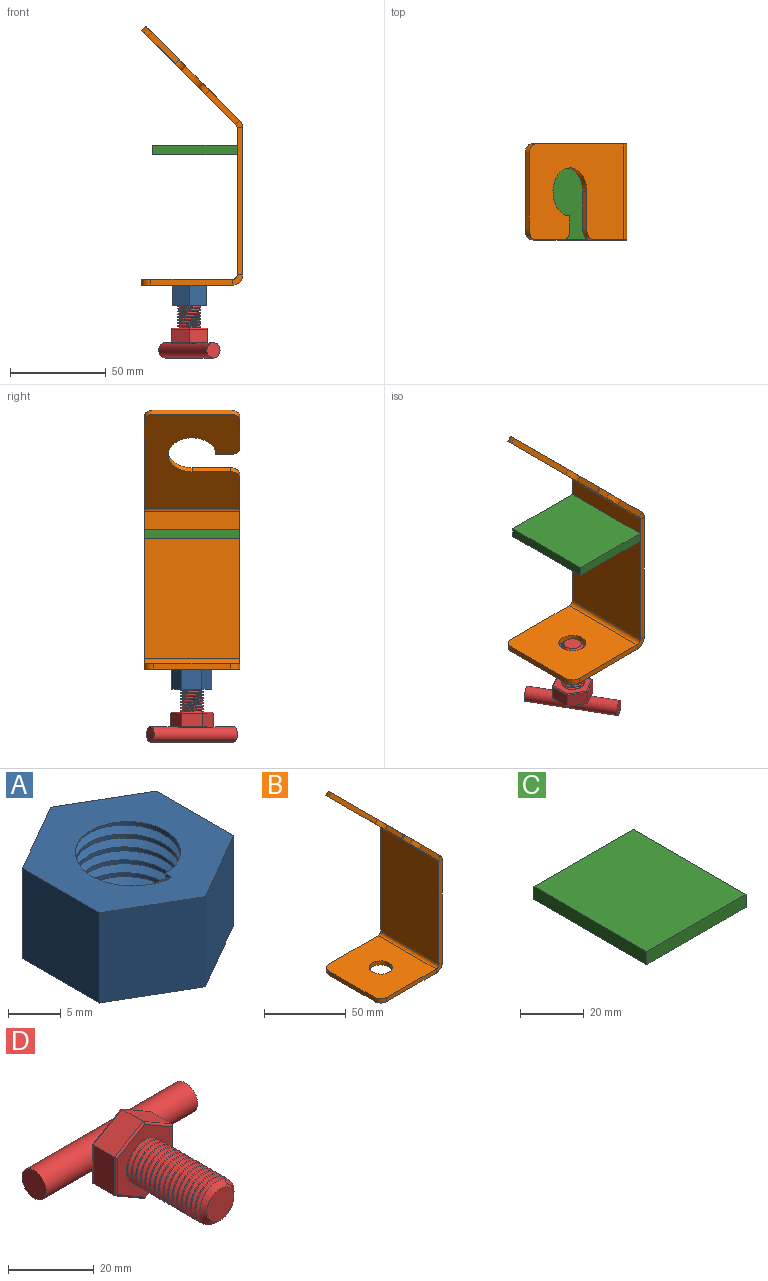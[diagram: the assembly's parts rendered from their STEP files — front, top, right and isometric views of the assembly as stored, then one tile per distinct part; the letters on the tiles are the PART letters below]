
ASSEMBLY  parts=4 mates=5
PART A: 13 faces, bbox 18.5x21.3x12.5 mm
  f0: cylinder r=5mm len=10.5mm, axis (0,0,-1), area 102.1mm2, adj f1,f8,f9,f10,f11,f12
  f1: plane 21.32x18.54mm, normal (0,0,-1), area 196.9mm2, adj f0,f2,f3,f4,f5,f6,f7,f9
  f2: plane 10.5x9mm, normal (-0.5,0.87,0), area 109.1mm2, adj f1,f3,f7,f8
  f3: plane 10.5x10.39mm, normal (-1,0,0), area 109.1mm2, adj f1,f2,f4,f8
  f4: plane 10.5x9mm, normal (-0.5,-0.87,0), area 109.1mm2, adj f1,f3,f5,f8
  f5: plane 10.5x9mm, normal (0.5,-0.87,0), area 109.1mm2, adj f1,f4,f6,f8
  f6: plane 10.5x10.39mm, normal (1,0,0), area 109.1mm2, adj f1,f5,f7,f8
  f7: plane 10.5x9mm, normal (0.5,0.87,0), area 109.1mm2, adj f1,f2,f6,f8
  f8: plane 21.32x18.54mm, normal (0,0,1), area 196.9mm2, adj f0,f2,f3,f4,f5,f6,f7,f10
  f9: plane 0.9x0.52mm, normal (1,0,0), area 0.2mm2, adj f0,f1,f11
  f10: plane 0.9x0.52mm, normal (-1,0,0), area 0.2mm2, adj f0,f8,f12
  f11: bspline ~13.63x11.8mm, area 243mm2, adj f0,f8,f9,f12
  f12: bspline ~13.63x11.8mm, area 240.1mm2, adj f0,f1,f10,f11
PART B: 33 faces, bbox 53x50x135.1 mm
  f0: plane 42.7x3mm, normal (0,-1,0), area 128.1mm2, adj f4,f5,f6,f30
  f1: plane 40x3mm, normal (-1,0,0), area 120mm2, adj f4,f5,f6,f7
  f2: plane 42.7x3mm, normal (0,1,0), area 128.1mm2, adj f4,f5,f7,f29
  f3: cylinder r=7mm len=14mm, axis (0,0,1), area 131.9mm2, adj f4,f5
  f4: plane 50x47.7mm, normal (0,0,-1), area 2220.3mm2, adj f0,f1,f2,f3,f6,f7,f31
  f5: plane 50x47.7mm, normal (0,0,1), area 2220.3mm2, adj f0,f1,f2,f3,f6,f7,f32
  f6: cylinder r=5mm len=5mm, axis (0,0,1), area 23.6mm2, adj f0,f1,f4,f5
  f7: cylinder r=5mm len=5mm, axis (0,0,-1), area 23.6mm2, adj f1,f2,f4,f5
  f8: plane 76.75x3mm, normal (0,-1,0), area 230.2mm2, adj f10,f11,f26,f30
  f9: plane 76.75x3mm, normal (0,1,0), area 230.2mm2, adj f10,f11,f25,f29
  f10: plane 76.75x50mm, normal (1,0,0), area 3837.4mm2, adj f8,f9,f27,f31
  f11: plane 76.75x50mm, normal (-1,0,0), area 3837.4mm2, adj f8,f9,f28,f32
  f12: plane 47.91x47.91mm, normal (0,1,0), area 194.3mm2, adj f19,f20,f21,f25
  f13: plane 40x2.12mm, normal (-0.71,0,0.71), area 120mm2, adj f19,f20,f21,f22
  f14: plane 16.26x16.26mm, normal (0,-1,0), area 60mm2, adj f19,f20,f22,f24
  f15: plane 7.5x2.12mm, normal (0.71,0,-0.71), area 22.5mm2, adj f16,f19,f20,f24
  f16: cylinder r=12.5mm len=25mm, axis (-0.71,0,-0.71), area 176.7mm2, adj f15,f17,f19,f20
  f17: plane 20x2.12mm, normal (-0.71,0,0.71), area 60mm2, adj f16,f19,f20,f23
  f18: plane 17.86x17.86mm, normal (0,-1,0), area 66.8mm2, adj f19,f20,f23,f26
  f19: plane 50x49.33mm, normal (0.71,0,0.71), area 2785.8mm2, adj f12,f13,f14,f15,f16,f17,f18,f21
  f20: plane 50x49.33mm, normal (-0.71,0,-0.71), area 2785.8mm2, adj f12,f13,f14,f15,f16,f17,f18,f21
  f21: cylinder r=5mm len=5.66mm, axis (-0.71,0,-0.71), area 23.6mm2, adj f12,f13,f19,f20
  f22: cylinder r=5mm len=5.66mm, axis (0.71,0,0.71), area 23.6mm2, adj f13,f14,f19,f20
  f23: cylinder r=5mm len=5.66mm, axis (0.71,0,0.71), area 23.6mm2, adj f17,f18,f19,f20
  f24: cylinder r=5mm len=5.66mm, axis (-0.71,0,-0.71), area 23.6mm2, adj f14,f15,f19,f20
  f25: plane 3.75x3.67mm, normal (0,1,0), area 9mm2, adj f9,f12,f27,f28
  f26: plane 3.75x3.67mm, normal (0,-1,0), area 9mm2, adj f8,f18,f27,f28
  f27: cylinder r=5.3mm len=50mm, axis (0,1,0), area 208.1mm2, adj f10,f19,f25,f26
  f28: cylinder r=2.3mm len=50mm, axis (0,1,0), area 90.3mm2, adj f11,f20,f25,f26
  f29: plane 5.3x5.3mm, normal (0,1,0), area 17.9mm2, adj f2,f9,f31,f32
  f30: plane 5.3x5.3mm, normal (0,-1,0), area 17.9mm2, adj f0,f8,f31,f32
  f31: cylinder r=5.3mm len=50mm, axis (0,1,0), area 416.3mm2, adj f4,f10,f29,f30
  f32: cylinder r=2.3mm len=50mm, axis (0,1,0), area 180.6mm2, adj f5,f11,f29,f30
PART C: 6 faces, bbox 43.9x50x5 mm
  f0: plane 50x5mm, normal (-1,0,0), area 250mm2, adj f1,f3,f4,f5
  f1: plane 50x43.9mm, normal (0,0,-1), area 2194.8mm2, adj f0,f2,f4,f5
  f2: plane 50x5mm, normal (1,0,0), area 250mm2, adj f1,f3,f4,f5
  f3: plane 50x43.9mm, normal (0,0,1), area 2194.8mm2, adj f0,f2,f4,f5
  f4: plane 43.9x5mm, normal (0,-1,0), area 219.5mm2, adj f0,f1,f2,f3
  f5: plane 43.9x5mm, normal (0,1,0), area 219.5mm2, adj f0,f1,f2,f3
PART D: 35 faces, bbox 52.9x43.8x24.9 mm
  f0: plane 18x8.46mm, normal (0,1,0), area 105.4mm2, adj f1,f29,f30,f31,f34
  f1: cylinder r=0.5mm len=9.75mm, axis (0.87,0,-0.5), area 8.4mm2, adj f0,f2,f29,f34
  f2: plane 9.5x7mm, normal (-0.5,0,-0.87), area 76.8mm2, adj f1,f3,f27,f28
  f3: plane 10.97x7mm, normal (-1,0,0), area 76.8mm2, adj f2,f4,f25,f26,f34
  f4: cylinder r=0.5mm len=5.49mm, axis (0,0,-1), area 3.4mm2, adj f3,f5,f24,f31
  f5: cylinder r=0.5mm len=9.75mm, axis (-0.87,0,-0.5), area 8.4mm2, adj f4,f6,f24,f25
  f6: cylinder r=0.5mm len=9.75mm, axis (-0.87,0,0.5), area 8.4mm2, adj f5,f7,f23,f24
  f7: cylinder r=0.5mm len=5.49mm, axis (0,0,1), area 3.4mm2, adj f6,f8,f24,f31
  f8: plane 10.97x7mm, normal (1,0,0), area 76.8mm2, adj f7,f9,f23,f28,f30
  f9: cylinder r=0.5mm len=10.97mm, axis (0,0,-1), area 8.4mm2, adj f8,f10,f11,f22
  f10: cylinder r=0.5mm len=9.75mm, axis (-0.87,0,-0.5), area 8.4mm2, adj f9,f11,f27,f28
  f11: plane 23.72x20.94mm, normal (0,-1,0), area 174.4mm2, adj f9,f10,f12,f18,f19,f20,f21,f22
  f12: cylinder r=6mm len=23.5mm, axis (0,1,0), area 256.6mm2, adj f11,f13,f16,f17,f18,f20
  f13: cone r=4.5mm half-angle=45deg, axis (0,1,0), area 7mm2, adj f12,f14,f16,f20
  f14: cone r=4.5mm half-angle=45deg, axis (0,1,0), area 43.5mm2, adj f13,f15,f16,f17
  f15: plane 9x9mm, normal (0,-1,0), area 63.6mm2, adj f14
  f16: bspline ~14.05x12.17mm, area 3.6mm2, adj f12,f13,f14
  f17: bspline ~24.13x14.05mm, area 200.6mm2, adj f12,f14,f18,f20
  f18: plane 3.72x3.43mm, normal (0.87,0,0.5), area 0.2mm2, adj f11,f12,f17
  f19: bspline ~10x9.99mm, area 0mm2, adj f11,f20
  f20: bspline ~25.63x14.05mm, area 640.5mm2, adj f11,f12,f13,f17,f19
  f21: cylinder r=0.5mm len=9.75mm, axis (0.87,0,0.5), area 8.4mm2, adj f11,f22,f25,f26
  f22: cylinder r=0.5mm len=9.75mm, axis (0.87,0,-0.5), area 8.4mm2, adj f9,f11,f21,f23
  f23: plane 9.5x7mm, normal (0.5,0,0.87), area 76.8mm2, adj f6,f8,f22,f25
  f24: plane 18x8.46mm, normal (0,1,0), area 105.4mm2, adj f4,f5,f6,f7,f31
  f25: plane 9.5x7mm, normal (-0.5,0,0.87), area 76.8mm2, adj f3,f5,f21,f23
  f26: cylinder r=0.5mm len=10.97mm, axis (0,0,1), area 8.4mm2, adj f3,f11,f21,f27
  f27: cylinder r=0.5mm len=9.75mm, axis (-0.87,0,0.5), area 8.4mm2, adj f2,f10,f11,f26
  f28: plane 9.5x7mm, normal (0.5,0,-0.87), area 76.8mm2, adj f2,f8,f10,f29
  f29: cylinder r=0.5mm len=9.75mm, axis (0.87,0,0.5), area 8.4mm2, adj f0,f1,f28,f30
  f30: cylinder r=0.5mm len=5.49mm, axis (0,0,1), area 3.4mm2, adj f0,f8,f29,f31
  f31: cylinder r=4mm len=50mm, axis (-1,0,0), area 1181.8mm2, adj f0,f4,f7,f24,f30,f32,f33,f34
  f32: plane 8x8mm, normal (-1,0,0), area 50.3mm2, adj f31
  f33: plane 8x8mm, normal (1,0,0), area 50.3mm2, adj f31
  f34: cylinder r=0.5mm len=5.49mm, axis (0,0,-1), area 3.4mm2, adj f0,f1,f3,f31
PLACE A rot(axis=(1,0,0),180deg) t=(-83.13,10.71,201.18)mm
PLACE B rot(axis=(-0.13,-0.07,0.99),0deg) t=(-108.21,35.61,204.18)mm
PLACE C t=(-102.1,35.61,269.18)mm
PLACE D rot(axis=(-0.38,-0.65,0.65),138.6deg) t=(-83.05,10.61,178.68)mm
MATE planar C.f4 <-> B.f8  axis (0,-1,0) through (-80.15,-14.39,271.68)mm
MATE cylindrical D.f12 <-> A.f8  axis (0,0,1) through (-83.05,10.61,203.68)mm
MATE parallel C.f3 <-> B.f5  axis (0,0,1) through (-80.15,10.61,274.18)mm
MATE planar B.f11 <-> C.f2  axis (-1,0,0) through (-58.21,10.61,244.85)mm
MATE fastened B.f3 <-> A.f1  axis (0,0,-1) through (-83.21,10.61,201.18)mm
